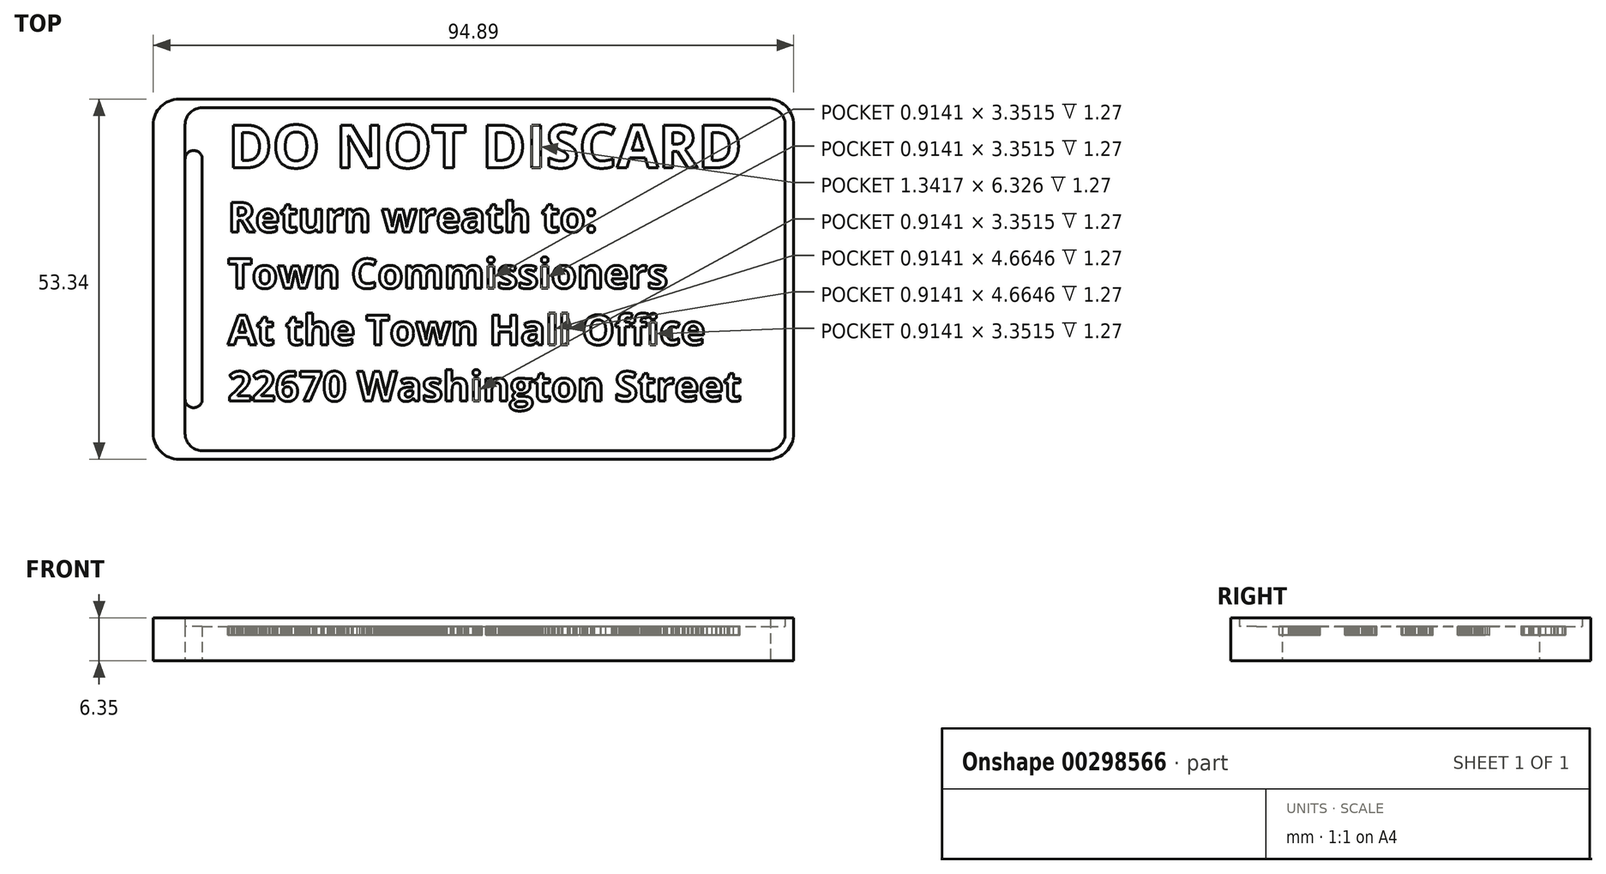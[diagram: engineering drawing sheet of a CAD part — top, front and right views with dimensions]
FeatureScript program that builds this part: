
annotation { "Feature Type Name" : "Feature", "Feature Type Description" : "" }
export const myFeature = defineFeature(function(context is Context, id is Id, definition is map)
    precondition{}
    {
        {
            var Q0;
            Q0=qCreatedBy(makeId("Top.planeOp"),FACE);
            var sketch = newSketch(context, id + "F0", { "sketchPlane" : qUnion([Q0])});
            skLineSegment(sketch, "E0.bottom", {"start": v(2.54, 0) * mm, "end": v(86.36, 0) * mm});
            skLineSegment(sketch, "E0.top", {"start": v(2.54, 50.8) * mm, "end": v(86.36, 50.8) * mm});
            skLineSegment(sketch, "E0.left", {"start": v(0, 2.54) * mm, "end": v(0, 48.26) * mm});
            skLineSegment(sketch, "E0.right", {"start": v(88.9, 2.54) * mm, "end": v(88.9, 48.26) * mm});
            skPoint(sketch, "E1.visualSharp", {"position": v(0, 50.8) * mm});
            skArc(sketch, "E1.filletArc", {"start": v(2.54, 50.8) * mm, "mid": v(0.74, 50.06) * mm, "end": v(0, 48.26) * mm});
            skPoint(sketch, "E2.visualSharp", {"position": v(88.9, 50.8) * mm});
            skArc(sketch, "E2.filletArc", {"start": v(88.9, 48.26) * mm, "mid": v(88.16, 50.06) * mm, "end": v(86.36, 50.8) * mm});
            skPoint(sketch, "E3.visualSharp", {"position": v(88.9, 0) * mm});
            skArc(sketch, "E3.filletArc", {"start": v(86.36, 0) * mm, "mid": v(88.16, 0.74) * mm, "end": v(88.9, 2.54) * mm});
            skPoint(sketch, "E4.visualSharp", {"position": v(0, 0) * mm});
            skArc(sketch, "E4.filletArc", {"start": v(0, 2.54) * mm, "mid": v(0.74, 0.74) * mm, "end": v(2.54, 0) * mm});
            skLineSegment(sketch, "E5.2", {"start": v(2.9, -1.27) * mm, "end": v(86.36, -1.27) * mm});
            skArc(sketch, "E5.4", {"start": v(86.36, -1.27) * mm, "mid": v(89.05, -0.15) * mm, "end": v(90.17, 2.54) * mm});
            skLineSegment(sketch, "E5.5", {"start": v(90.17, 2.54) * mm, "end": v(90.17, 48.26) * mm});
            skArc(sketch, "E5.6", {"start": v(90.17, 48.26) * mm, "mid": v(89.18, 50.84) * mm, "end": v(86.72, 52.07) * mm});
            skLineSegment(sketch, "E5.7", {"start": v(2.9, 52.07) * mm, "end": v(86.72, 52.07) * mm});
            skLineSegment(sketch, "E6", {"start": v(2.9, 52.07) * mm, "end": v(-0.91, 52.07) * mm});
            skLineSegment(sketch, "E7", {"start": v(2.9, -1.27) * mm, "end": v(-0.91, -1.27) * mm});
            skLineSegment(sketch, "E8", {"start": v(-4.72, 2.54) * mm, "end": v(-4.72, 48.26) * mm});
            skPoint(sketch, "E9.visualSharp", {"position": v(-4.72, 52.07) * mm});
            skArc(sketch, "E9.filletArc", {"start": v(-0.91, 52.07) * mm, "mid": v(-3.6, 50.96) * mm, "end": v(-4.72, 48.26) * mm});
            skPoint(sketch, "E10.visualSharp", {"position": v(-4.72, -1.27) * mm});
            skArc(sketch, "E10.filletArc", {"start": v(-4.72, 2.54) * mm, "mid": v(-3.6, -0.15) * mm, "end": v(-0.91, -1.27) * mm});
            skLineSegment(sketch, "E11", {"start": v(0, 25.4) * mm, "end": v(67.57, 25.4) * mm, "construction": true});
            skPoint(sketch, "E11.endSnap0", {"position": v(0, 25.4) * mm});
            skArc(sketch, "E12", {"start": v(2.54, 43.18) * mm, "mid": v(1.27, 44.45) * mm, "end": v(0, 43.18) * mm});
            skPoint(sketch, "E12.first.point", {"position": v(0, 43.18) * mm});
            skPoint(sketch, "E12.second.point", {"position": v(2.54, 43.18) * mm});
            skLineSegment(sketch, "E13", {"start": v(2.54, 43.18) * mm, "end": v(2.54, 25.4) * mm});
            skLineSegment(sketch, "E14.MirrorCS", {"start": v(2.54, 7.62) * mm, "end": v(2.54, 25.4) * mm});
            skArc(sketch, "E15.MirrorCS", {"start": v(2.54, 7.62) * mm, "mid": v(1.27, 6.35) * mm, "end": v(0, 7.62) * mm});
            skSolve(sketch);
        }
        {
            var Q0;
            Q0=makeQuery(id+"F0.imprint","IMPRINT",FACE,{"disambiguationData":[TD([[makeQuery(id+"F0.imprint","IMPRINT",EDGE,{"derivedFrom":sQuery(id+"F0.wireOp",EDGE,"E0.bottom")}),-1.0]])]});
            extrude(context, id + "F1", {"entities" : qUnion([Q0]), "depth" : 6.35 * mm});
        }
        {
            var Q0;
            Q0=makeQuery(id+"F0.imprint","IMPRINT",FACE,{"disambiguationData":[TD([[makeQuery(id+"F0.imprint","IMPRINT",EDGE,{"derivedFrom":sQuery(id+"F0.wireOp",EDGE,"E0.bottom")}),1.0]])]});
            extrude(context, id + "F2", {"entities" : qUnion([Q0]), "operationType" : NewBodyOperationType.ADD, "depth" : 5.08 * mm});
        }
        {
            var Q0;
            Q0=makeQuery(id+"F2.opExtrude","CAP_FACE",FACE,{"disambiguationData":[OSD([sQuery(id+"F0.wireOp",EDGE,"E0.bottom"),sQuery(id+"F0.wireOp",EDGE,"E0.top"),sQuery(id+"F0.wireOp",EDGE,"E0.left"),sQuery(id+"F0.wireOp",EDGE,"E0.right"),sQuery(id+"F0.wireOp",EDGE,"E1.filletArc"),sQuery(id+"F0.wireOp",EDGE,"E2.filletArc"),sQuery(id+"F0.wireOp",EDGE,"E3.filletArc"),sQuery(id+"F0.wireOp",EDGE,"E4.filletArc"),sQuery(id+"F0.wireOp",EDGE,"E12"),sQuery(id+"F0.wireOp",EDGE,"E13"),sQuery(id+"F0.wireOp",EDGE,"E14.MirrorCS"),sQuery(id+"F0.wireOp",EDGE,"E15.MirrorCS")])],"isStart":false});
            var sketch = newSketch(context, id + "F3", { "sketchPlane" : qUnion([Q0])});
            skText(sketch, "E16", { "text": "DO NOT DISCARD", "fontName": "OpenSans-Bold.ttf"});
            skText(sketch, "E17", { "text": "Return wreath to:\nTown Commissioners \nAt the Town Hall Office\n22670 Washington Street\n", "fontName": "OpenSans-Bold.ttf"});
            const initialGuessF3  = {"E16": [0.00635, 0.04188, 1, 0, 0.00638], "E17": [0.00635, 0.03238, 1, 0, 0.00442]};
            skSetInitialGuess(sketch, initialGuessF3);
            skSolve(sketch);
        }
        {
            var Q0;
            Q0=qSketchRegion(id+"F3",true);
            extrude(context, id + "F4", {"entities" : qUnion([Q0]), "operationType" : NewBodyOperationType.REMOVE, "oppositeDirection" : true, "depth" : 1.27 * mm});
        }
    });
